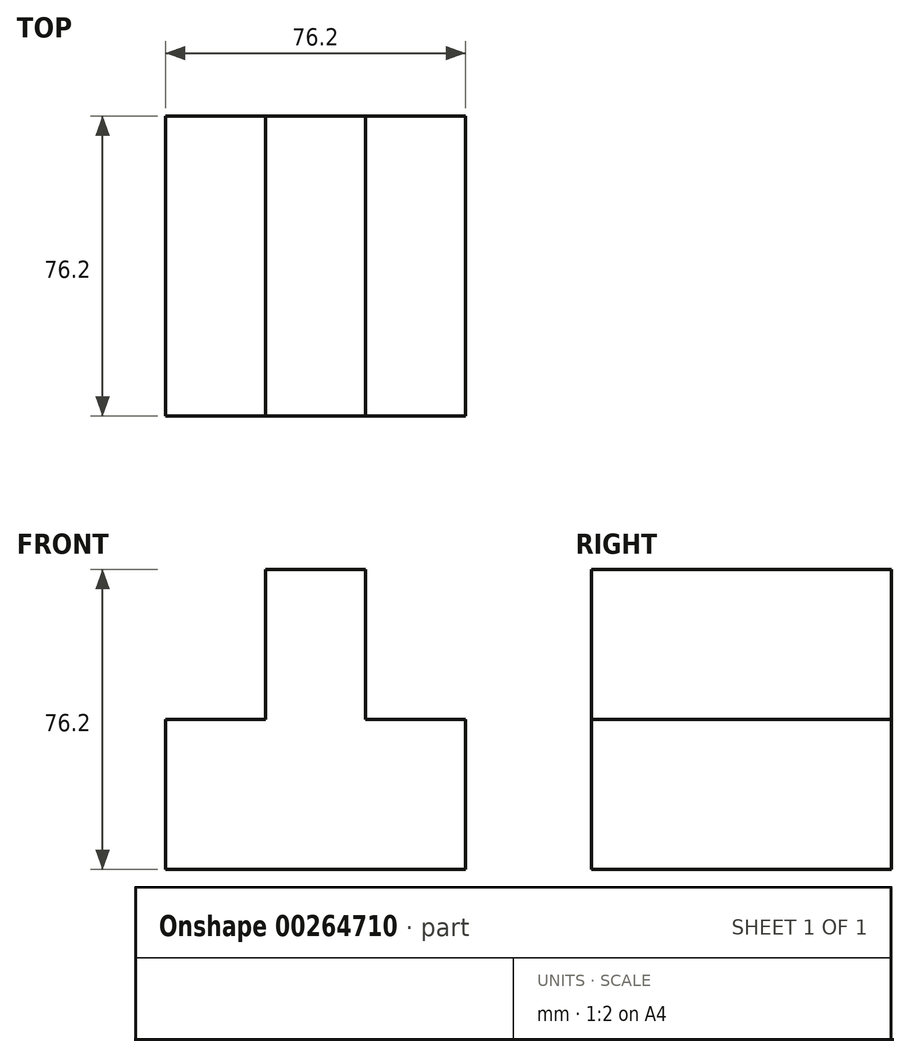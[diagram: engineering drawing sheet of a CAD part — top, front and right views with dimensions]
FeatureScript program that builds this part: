
annotation { "Feature Type Name" : "Feature", "Feature Type Description" : "" }
export const myFeature = defineFeature(function(context is Context, id is Id, definition is map)
    precondition{}
    {
        {
            var Q0;
            Q0=qCreatedBy(makeId("Front.planeOp"),FACE);
            var sketch = newSketch(context, id + "F0", { "sketchPlane" : qUnion([Q0])});
            skLineSegment(sketch, "E0", {"start": v(0, 0) * mm, "end": v(-76.2, 0) * mm});
            skLineSegment(sketch, "E1", {"start": v(-76.2, 0) * mm, "end": v(-76.2, 38.1) * mm});
            skLineSegment(sketch, "E2", {"start": v(-76.2, 38.1) * mm, "end": v(-50.8, 38.1) * mm});
            skLineSegment(sketch, "E3", {"start": v(-50.8, 38.1) * mm, "end": v(-50.8, 76.2) * mm});
            skLineSegment(sketch, "E4", {"start": v(-50.8, 76.2) * mm, "end": v(-25.4, 76.2) * mm});
            skLineSegment(sketch, "E5", {"start": v(-25.4, 76.2) * mm, "end": v(-25.4, 38.1) * mm});
            skLineSegment(sketch, "E6", {"start": v(-25.4, 38.1) * mm, "end": v(0, 38.1) * mm});
            skLineSegment(sketch, "E7", {"start": v(0, 38.1) * mm, "end": v(0, 0) * mm});
            skSolve(sketch);
        }
        {
            var Q0;
            Q0 = qSketchRegion(id + "F0", true);
            extrude(context, id + "F1", {"entities" : qUnion([Q0]), "depth" : 76.2 * mm});
        }
    });
